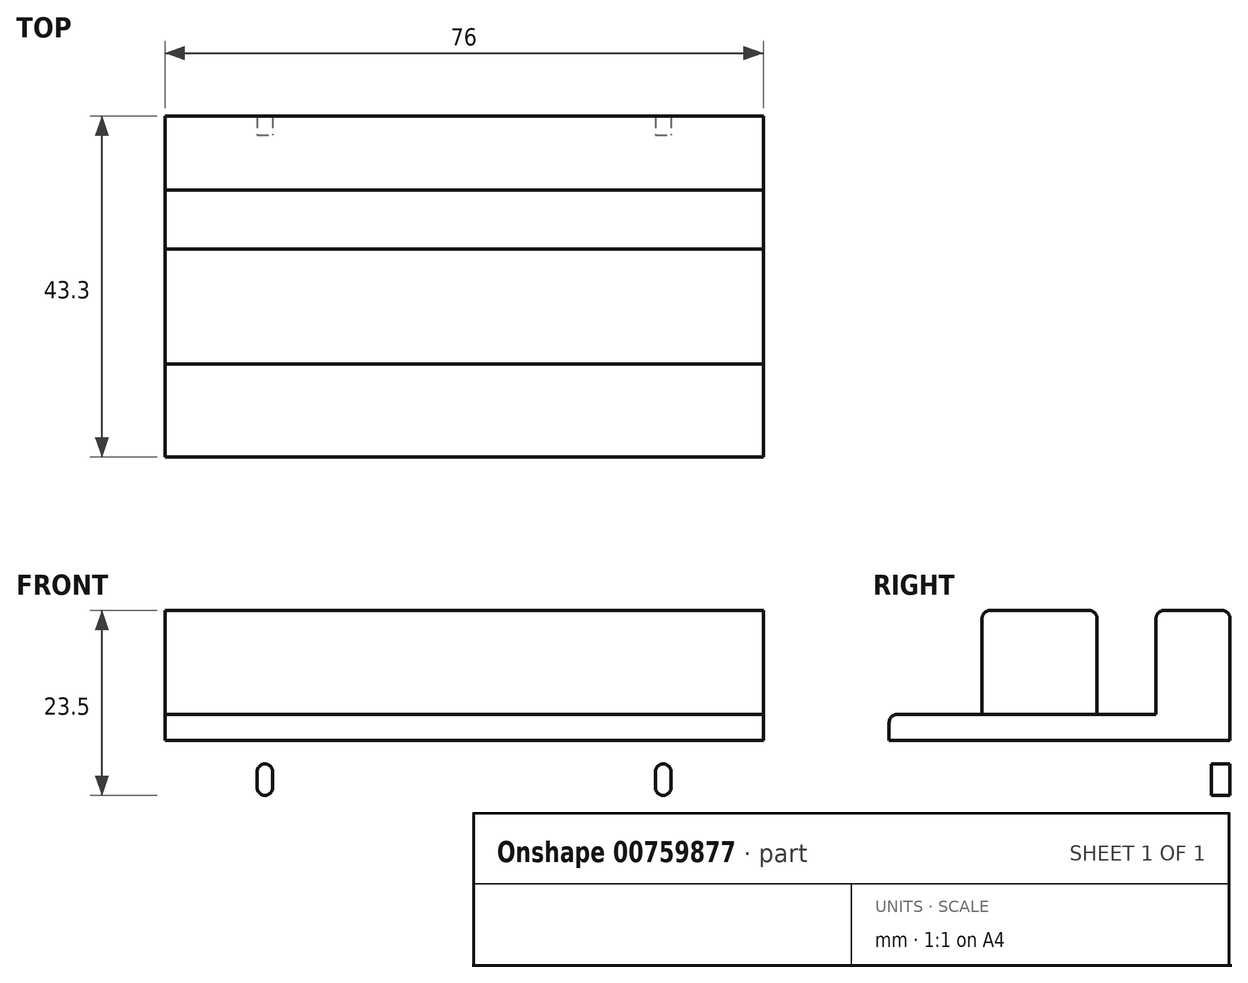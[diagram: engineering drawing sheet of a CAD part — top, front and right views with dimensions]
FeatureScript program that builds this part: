
annotation { "Feature Type Name" : "Feature", "Feature Type Description" : "" }
export const myFeature = defineFeature(function(context is Context, id is Id, definition is map)
    precondition{}
    {
        {
            var Q0;
            Q0=qCreatedBy(makeId("Top.planeOp"),FACE);
            var sketch = newSketch(context, id + "F0", { "sketchPlane" : qUnion([Q0])});
            skLineSegment(sketch, "E0.bottom", {"start": v(0, 0) * mm, "end": v(76, 0) * mm});
            skLineSegment(sketch, "E0.top", {"start": v(0, -43.3) * mm, "end": v(76, -43.3) * mm});
            skLineSegment(sketch, "E0.left", {"start": v(0, 0) * mm, "end": v(0, -43.3) * mm});
            skLineSegment(sketch, "E0.right", {"start": v(76, 0) * mm, "end": v(76, -43.3) * mm});
            skLineSegment(sketch, "E1", {"start": v(0, -9.4) * mm, "end": v(76, -9.4) * mm});
            skLineSegment(sketch, "E2", {"start": v(0, -16.9) * mm, "end": v(76, -16.9) * mm});
            skLineSegment(sketch, "E3", {"start": v(0, -31.5) * mm, "end": v(76, -31.5) * mm});
            skLineSegment(sketch, "E4", {"start": v(0, -2.4) * mm, "end": v(76, -2.4) * mm});
            skSolve(sketch);
        }
        {
            var Q0;
            {var subQ0=sQuery(id+"F0.wireOp",EDGE,"E1");Q0=makeQuery(id+"F0.imprint","IMPRINT",FACE,{"disambiguationData":[TD([[makeQuery(id+"F0.imprint","IMPRINT",EDGE,{"derivedFrom":subQ0}),1.0]])]});}
            var Q1;
            {var subQ0=sQuery(id+"F0.wireOp",EDGE,"E0.bottom");Q1=makeQuery(id+"F0.imprint","IMPRINT",FACE,{"disambiguationData":[TD([[makeQuery(id+"F0.imprint","IMPRINT",EDGE,{"derivedFrom":subQ0}),-1.0]])]});}
            var Q2;
            {var subQ0=sQuery(id+"F0.wireOp",EDGE,"E2");Q2=makeQuery(id+"F0.imprint","IMPRINT",FACE,{"disambiguationData":[TD([[makeQuery(id+"F0.imprint","IMPRINT",EDGE,{"derivedFrom":subQ0}),-1.0]])]});}
            extrude(context, id + "F1", {"entities" : qUnion([Q0, Q1, Q2]), "depth" : 13.2 * mm, "offsetDistance" : 25 * mm});
        }
        {
            var Q0;
            {var subQ0=sQuery(id+"F0.wireOp",EDGE,"E1");Q0=makeQuery(id+"F0.imprint","IMPRINT",FACE,{"disambiguationData":[TD([[makeQuery(id+"F0.imprint","IMPRINT",EDGE,{"derivedFrom":subQ0}),1.0]])]});}
            var Q1;
            {var subQ0=sQuery(id+"F0.wireOp",EDGE,"E1");Q1=makeQuery(id+"F0.imprint","IMPRINT",FACE,{"disambiguationData":[TD([[makeQuery(id+"F0.imprint","IMPRINT",EDGE,{"derivedFrom":subQ0}),-1.0]])]});}
            var Q2;
            {var subQ0=sQuery(id+"F0.wireOp",EDGE,"E2");Q2=makeQuery(id+"F0.imprint","IMPRINT",FACE,{"disambiguationData":[TD([[makeQuery(id+"F0.imprint","IMPRINT",EDGE,{"derivedFrom":subQ0}),-1.0]])]});}
            var Q3;
            {var subQ0=sQuery(id+"F0.wireOp",EDGE,"E0.top");Q3=makeQuery(id+"F0.imprint","IMPRINT",FACE,{"disambiguationData":[TD([[makeQuery(id+"F0.imprint","IMPRINT",EDGE,{"derivedFrom":subQ0}),1.0]])]});}
            extrude(context, id + "F2", {"entities" : qUnion([Q0, Q1, Q2, Q3]), "oppositeDirection" : true, "depth" : 3.3 * mm, "offsetDistance" : 25 * mm});
        }
        {
            var Q0;
            {var subQ0=sQuery(id+"F0.wireOp",EDGE,"E0.bottom");Q0=makeQuery(id+"F0.imprint","IMPRINT",FACE,{"disambiguationData":[TD([[makeQuery(id+"F0.imprint","IMPRINT",EDGE,{"derivedFrom":subQ0}),-1.0]])]});}
            extrude(context, id + "F3", {"entities" : qUnion([Q0]), "operationType" : NewBodyOperationType.ADD, "oppositeDirection" : true, "depth" : 14 * mm, "offsetDistance" : 25 * mm});
        }
        {
            var Q0;
            Q0=makeQuery(id+"F1.opExtrude","CAP_EDGE",EDGE,{"disambiguationData":[OSD([sQuery(id+"F0.wireOp",EDGE,"E0.bottom")])],"isStart":false});
            var Q1;
            Q1=makeQuery(id+"F1.opExtrude","CAP_EDGE",EDGE,{"disambiguationData":[OSD([sQuery(id+"F0.wireOp",EDGE,"E1")])],"isStart":false});
            var Q2;
            Q2=makeQuery(id+"F1.opExtrude","CAP_EDGE",EDGE,{"disambiguationData":[OSD([sQuery(id+"F0.wireOp",EDGE,"E2")])],"isStart":false});
            var Q3;
            Q3=makeQuery(id+"F1.opExtrude","CAP_EDGE",EDGE,{"disambiguationData":[OSD([sQuery(id+"F0.wireOp",EDGE,"E3")])],"isStart":false});
            fillet(context, id + "F4", {"entities" : qUnion([Q0, Q1, Q2, Q3]), "radius" : 1 * mm, "tangentPropagation" : true, "allowEdgeOverflow" : false});
        }
        {
            var Q0;
            Q0=makeQuery(id+"F3.opExtrude","CAP_EDGE",EDGE,{"disambiguationData":[OSD([sQuery(id+"F0.wireOp",EDGE,"E0.bottom")])],"isStart":false});
            fillet(context, id + "F5", {"entities" : qUnion([Q0]), "radius" : 1 * mm, "tangentPropagation" : true, "allowEdgeOverflow" : false});
        }
        {
            var Q0;
            Q0=makeQuery(id+"F2.opExtrude","CAP_EDGE",EDGE,{"disambiguationData":[OSD([sQuery(id+"F0.wireOp",EDGE,"E0.top")])],"isStart":true});
            fillet(context, id + "F6", {"entities" : qUnion([Q0]), "radius" : 1 * mm, "tangentPropagation" : true, "allowEdgeOverflow" : false});
        }
        {
            var Q0;
            Q0=makeQuery(id+"F3.opExtrude","SWEPT_FACE",FACE,{"disambiguationData":[OSD([sQuery(id+"F0.wireOp",EDGE,"E4")])]});
            var sketch = newSketch(context, id + "F7", { "sketchPlane" : qUnion([Q0])});
            skLineSegment(sketch, "E5", {"start": v(12.7, -9.3) * mm, "end": v(63.3, -9.3) * mm, "construction": true});
            skLineSegment(sketch, "E6", {"start": v(38, -14) * mm, "end": v(38, -3.29) * mm, "construction": true});
            skLineSegment(sketch, "E7", {"start": v(12.7, -9.3) * mm, "end": v(12.7, -7.3) * mm, "construction": true});
            skLineSegment(sketch, "E8", {"start": v(63.3, -9.3) * mm, "end": v(63.3, -7.3) * mm, "construction": true});
            skArc(sketch, "E9.0.startCap", {"start": v(13.7, -9.3) * mm, "mid": v(12.7, -10.3) * mm, "end": v(11.7, -9.3) * mm});
            skArc(sketch, "E9.0.endCap", {"start": v(11.7, -7.3) * mm, "mid": v(12.7, -6.3) * mm, "end": v(13.7, -7.3) * mm});
            skLineSegment(sketch, "E9.0.left", {"start": v(11.7, -9.3) * mm, "end": v(11.7, -7.3) * mm});
            skLineSegment(sketch, "E9.0.right", {"start": v(13.7, -9.3) * mm, "end": v(13.7, -7.3) * mm});
            skArc(sketch, "E9.1.startCap", {"start": v(64.3, -9.3) * mm, "mid": v(63.3, -10.3) * mm, "end": v(62.3, -9.3) * mm});
            skArc(sketch, "E9.1.endCap", {"start": v(62.3, -7.3) * mm, "mid": v(63.3, -6.3) * mm, "end": v(64.3, -7.3) * mm});
            skLineSegment(sketch, "E9.1.left", {"start": v(62.3, -9.3) * mm, "end": v(62.3, -7.3) * mm});
            skLineSegment(sketch, "E9.1.right", {"start": v(64.3, -9.3) * mm, "end": v(64.3, -7.3) * mm});
            skSolve(sketch);
        }
        {
            var Q0;
            Q0=makeQuery(id+"F7.imprint","IMPRINT",FACE,{"disambiguationData":[TD([[makeQuery(id+"F7.imprint","IMPRINT",EDGE,{"derivedFrom":sQuery(id+"F7.wireOp",EDGE,"E9.0.startCap")}),-1.0]])]});
            var Q1;
            Q1=makeQuery(id+"F7.imprint","IMPRINT",FACE,{"disambiguationData":[TD([[makeQuery(id+"F7.imprint","IMPRINT",EDGE,{"derivedFrom":sQuery(id+"F7.wireOp",EDGE,"E9.1.startCap")}),-1.0]])]});
            extrude(context, id + "F8", {"entities" : qUnion([Q0, Q1]), "operationType" : NewBodyOperationType.REMOVE, "endBound" : BoundingType.THROUGH_ALL, "oppositeDirection" : true, "depth" : 25 * mm, "offsetDistance" : 25 * mm});
        }
    });
